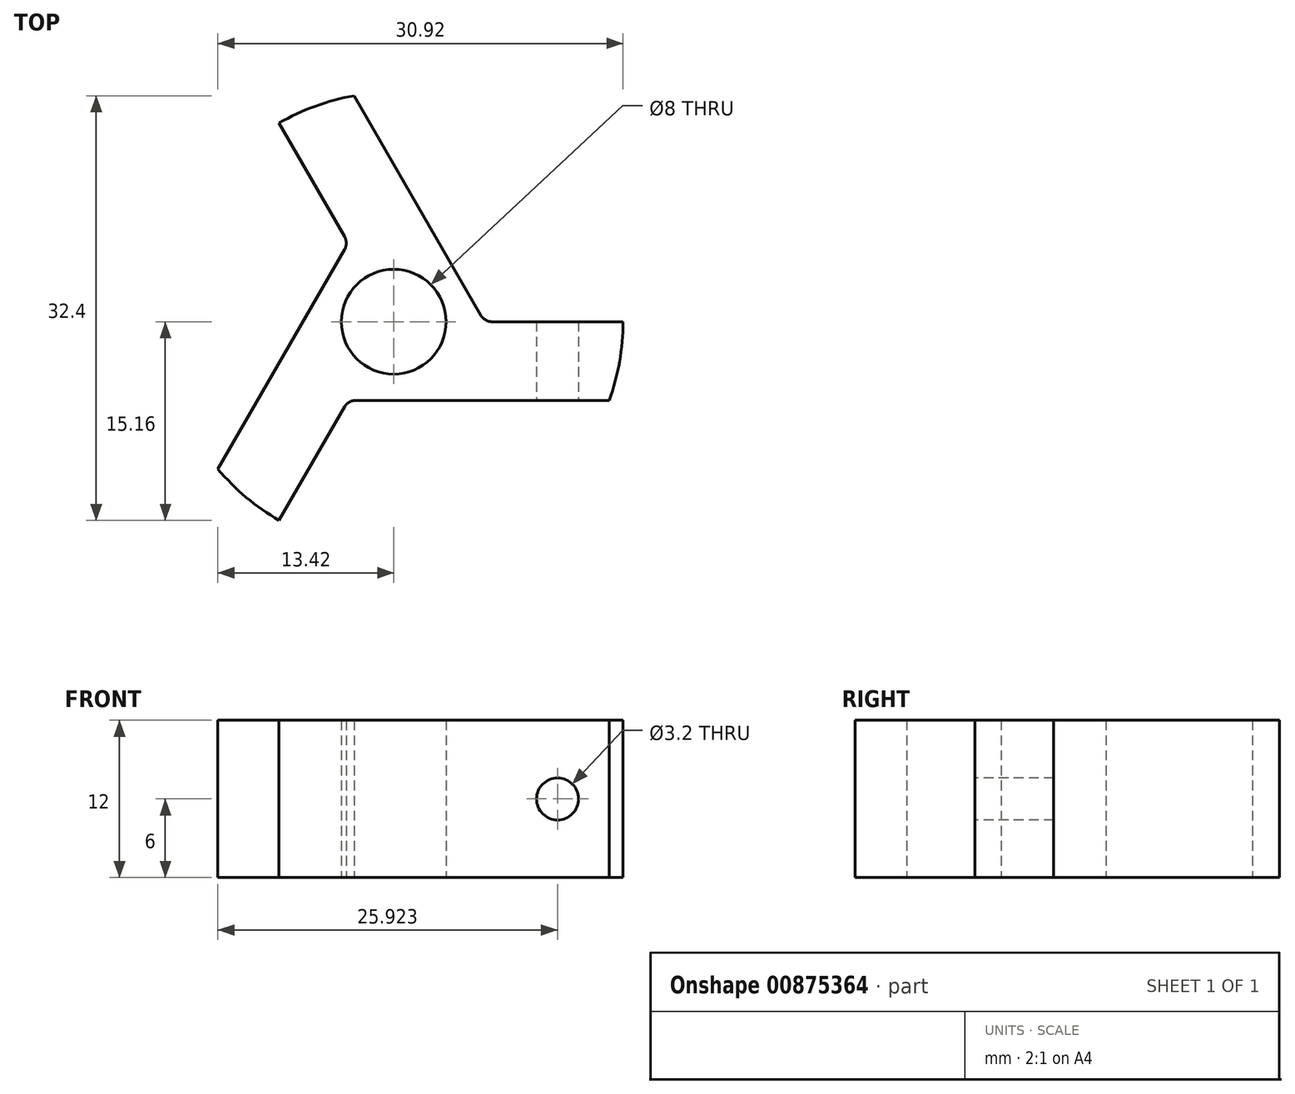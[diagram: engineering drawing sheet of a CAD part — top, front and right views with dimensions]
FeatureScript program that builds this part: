
annotation { "Feature Type Name" : "Feature", "Feature Type Description" : "" }
export const myFeature = defineFeature(function(context is Context, id is Id, definition is map)
    precondition{}
    {
        {
            var Q0;
            Q0=qCreatedBy(makeId("Top.planeOp"),FACE);
            var sketch = newSketch(context, id + "F0", { "sketchPlane" : qUnion([Q0])});
            skCircle(sketch, "E0", {"center": v(0, 0) * mm, "radius": 17.5 * mm, "construction": true});
            skCircle(sketch, "E1", {"center": v(0, 0) * mm, "radius": 4 * mm});
            skPoint(sketch, "E2", {"position": v(3.04, 17.23) * mm});
            skArc(sketch, "E3", {"start": v(6, 16.44) * mm, "mid": v(3.05, 17.23) * mm, "end": v(0, 17.5) * mm});
            skArc(sketch, "E4.1.2", {"start": v(-16.44, 6) * mm, "mid": v(-17.23, 3.05) * mm, "end": v(-17.5, 0) * mm});
            skPoint(sketch, "E4.1.3", {"position": v(-17.23, 3.04) * mm});
            skArc(sketch, "E4.3.2", {"start": v(16.44, -6) * mm, "mid": v(17.23, -3.05) * mm, "end": v(17.5, 0) * mm});
            skPoint(sketch, "E4.3.3", {"position": v(17.23, -3.04) * mm});
            skCircle(sketch, "E5.0", {"center": v(0, 0) * mm, "radius": 6 * mm, "construction": true});
            skArc(sketch, "E6.1.1", {"start": v(-3.02, 17.24) * mm, "mid": v(-5.98, 16.45) * mm, "end": v(-8.75, 15.16) * mm});
            skLineSegment(sketch, "E7", {"start": v(16.44, -6) * mm, "end": v(-2.89, -6) * mm});
            skLineSegment(sketch, "E8", {"start": v(-3.75, -6.5) * mm, "end": v(-8.75, -15.16) * mm});
            skPoint(sketch, "E9.1.1", {"position": v(-5.98, 16.45) * mm});
            skLineSegment(sketch, "E9.1.2", {"start": v(-3.02, 17.24) * mm, "end": v(6.64, 0.5) * mm});
            skLineSegment(sketch, "E9.1.3", {"start": v(7.5, 0) * mm, "end": v(17.5, 0) * mm});
            skArc(sketch, "E9.2.0", {"start": v(-13.42, -11.24) * mm, "mid": v(-11.25, -13.4) * mm, "end": v(-8.75, -15.16) * mm});
            skPoint(sketch, "E9.2.1", {"position": v(-11.25, -13.4) * mm});
            skLineSegment(sketch, "E9.2.2", {"start": v(-13.42, -11.24) * mm, "end": v(-3.75, 5.5) * mm});
            skLineSegment(sketch, "E9.2.3", {"start": v(-3.75, 6.5) * mm, "end": v(-8.75, 15.16) * mm});
            skPoint(sketch, "E10.visualSharp", {"position": v(6.93, 0) * mm});
            skArc(sketch, "E10.filletArc", {"start": v(6.64, 0.5) * mm, "mid": v(7, 0.13) * mm, "end": v(7.5, 0) * mm});
            skPoint(sketch, "E11.visualSharp", {"position": v(-3.46, -6) * mm});
            skArc(sketch, "E11.filletArc", {"start": v(-2.89, -6) * mm, "mid": v(-3.39, -6.13) * mm, "end": v(-3.75, -6.5) * mm});
            skPoint(sketch, "E12.visualSharp", {"position": v(-3.46, 6) * mm});
            skArc(sketch, "E12.filletArc", {"start": v(-3.75, 5.5) * mm, "mid": v(-3.62, 6) * mm, "end": v(-3.75, 6.5) * mm});
            skSolve(sketch);
        }
        {
            var Q0;
            Q0=makeQuery(id+"F0.imprint","IMPRINT",FACE,{"disambiguationData":[TD([[makeQuery(id+"F0.imprint","IMPRINT",EDGE,{"derivedFrom":sQuery(id+"F0.wireOp",EDGE,"E1")}),-1.0]])]});
            extrude(context, id + "F1", {"entities" : qUnion([Q0]), "depth" : 12 * mm, "offsetDistance" : 25 * mm});
        }
        {
            var Q0;
            Q0=makeQuery(id+"F1.opExtrude","SWEPT_FACE",FACE,{"disambiguationData":[OSD([sQuery(id+"F0.wireOp",EDGE,"E9.1.3")])]});
            var sketch = newSketch(context, id + "F2", { "sketchPlane" : qUnion([Q0])});
            skPoint(sketch, "E13", {"position": v(-12.5, 6) * mm});
            skLineSegment(sketch, "E14", {"start": v(-7.5, 0) * mm, "end": v(-17.5, 12) * mm, "construction": true});
            skLineSegment(sketch, "E15", {"start": v(-17.5, 0) * mm, "end": v(-7.5, 12) * mm, "construction": true});
            skSolve(sketch);
        }
        {
            var Q0;
            Q0=sQuery(id+"F2.wireOp",VERTEX,"E13");
            var Q1;
            Q1=makeQuery(id+"F1.opExtrude","SWEPT_BODY",BODY,{"disambiguationData":[OSD([sQuery(id+"F0.wireOp",EDGE,"E1"),sQuery(id+"F0.wireOp",EDGE,"97UaODRb-1AAY-LL8U-D3WL-IL7lug5A3xzh"),sQuery(id+"F0.wireOp",EDGE,"eU1vWybg-saEf-OJkc-mFlj-TbWGaT4ko4F4"),sQuery(id+"F0.wireOp",EDGE,"E3"),sQuery(id+"F0.wireOp",EDGE,"E4.1.0"),sQuery(id+"F0.wireOp",EDGE,"E4.1.1"),sQuery(id+"F0.wireOp",EDGE,"E4.1.2"),sQuery(id+"F0.wireOp",EDGE,"E4.2.0"),sQuery(id+"F0.wireOp",EDGE,"E4.2.1"),sQuery(id+"F0.wireOp",EDGE,"E4.2.2"),sQuery(id+"F0.wireOp",EDGE,"E4.3.0"),sQuery(id+"F0.wireOp",EDGE,"E4.3.1"),sQuery(id+"F0.wireOp",EDGE,"E4.3.2"),sQuery(id+"F0.wireOp",EDGE,"dbcb2a29-e490-407e-a6d4-f7dbf82e4c67.filletArc"),sQuery(id+"F0.wireOp",EDGE,"3a5a9858-2623-4842-a4ca-5da1a7be2698.filletArc"),sQuery(id+"F0.wireOp",EDGE,"4f9f7175-1fee-48e9-9383-dcedd981e3ce.filletArc"),sQuery(id+"F0.wireOp",EDGE,"4ae89ab7-3df8-49ff-89ba-0655c21711d6.filletArc")])]});
            hole(context, id + "F3", {"style" : HoleStyle.SIMPLE, "endStyle" : HoleEndStyle.BLIND, "standardTappedOrClearance" : lookupTablePath({ "fit" : "Close", "standard" : "ISO", "size" : "M3", "type" : "Clearance" }), "standardBlindInLast" : lookupTablePath({ "fit" : "Close", "standard" : "ISO", "engagement" : "75%", "pitch" : "0.5 mm", "size" : "M3", "type" : "Clearance & tapped" }), "holeDiameter" : 3.2 * mm, "majorDiameter" : 5 * mm, "holeDepth" : 6 * mm, "isTappedThrough" : true, "tappedDepth" : 12 * mm, "tapClearance" : 3, "locations" : qUnion([Q0]), "scope" : qUnion([Q1]), "startStyle" : HoleStartStyle.SKETCH});
        }
        {
            var Q0;
            Q0=qCreatedBy(makeId("Front.planeOp"),FACE);
            var sketch = newSketch(context, id + "F4", { "sketchPlane" : qUnion([Q0])});
            skLineSegment(sketch, "E16", {"start": v(0, 48.58) * mm, "end": v(0, -38.1) * mm, "construction": true});
            skSolve(sketch);
        }
    });
